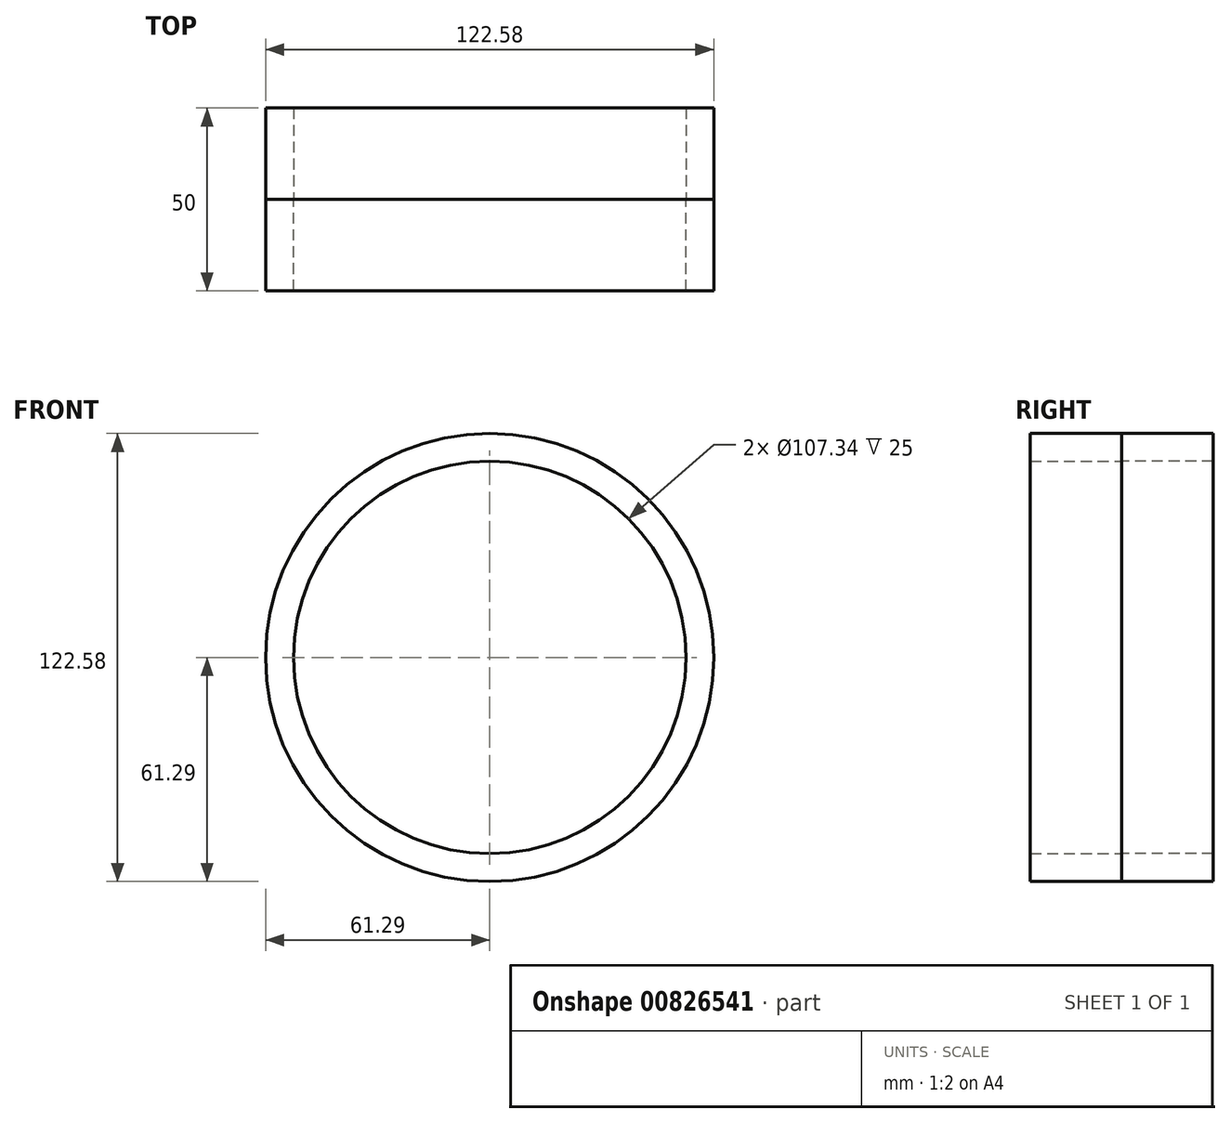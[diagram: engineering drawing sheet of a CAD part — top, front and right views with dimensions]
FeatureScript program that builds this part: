
annotation { "Feature Type Name" : "Feature", "Feature Type Description" : "" }
export const myFeature = defineFeature(function(context is Context, id is Id, definition is map)
    precondition{}
    {
        {
            var Q0;
            Q0=qCreatedBy(makeId("Front.planeOp"),FACE);
            var sketch = newSketch(context, id + "F0", { "sketchPlane" : qUnion([Q0])});
            skCircle(sketch, "E0", {"center": v(0, 0) * mm, "radius": 26.2 * mm});
            skCircle(sketch, "E1", {"center": v(0, 0) * mm, "radius": 53.67 * mm});
            skCircle(sketch, "E2", {"center": v(0, 0) * mm, "radius": 61.3 * mm});
            skSolve(sketch);
        }
        {
            var Q0;
            Q0=makeQuery(id+"F0.imprint","IMPRINT",FACE,{"disambiguationData":[TD([[makeQuery(id+"F0.imprint","IMPRINT",EDGE,{"derivedFrom":sQuery(id+"F0.wireOp",EDGE,"E1")}),-1.0]])]});
            extrude(context, id + "F1", {"entities" : qUnion([Q0]), "depth" : 25 * mm, "offsetDistance" : 25 * mm});
        }
        {
            var Q0;
            Q0 = qSketchRegion(id + "F0", true);
            extrude(context, id + "F2", {"entities" : qUnion([Q0]), "oppositeDirection" : true, "depth" : 25 * mm, "offsetDistance" : 25 * mm});
        }
    });
